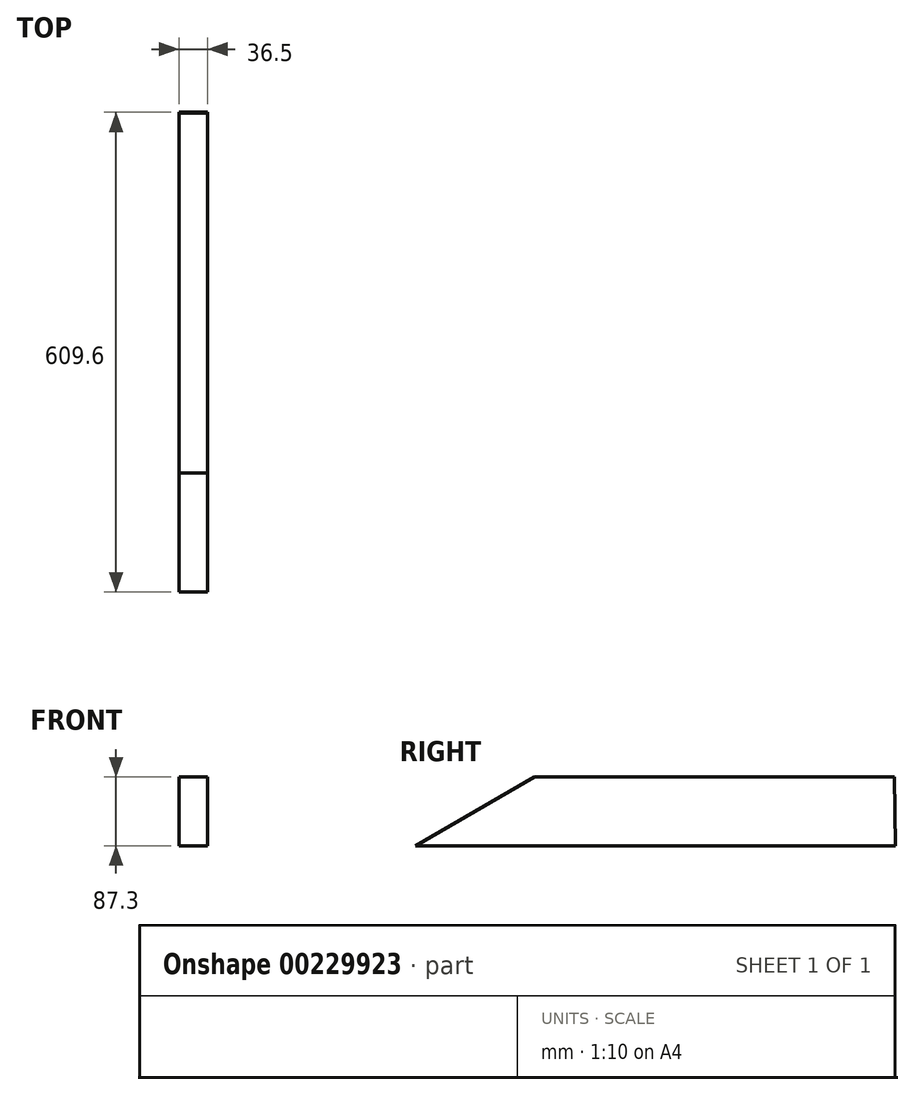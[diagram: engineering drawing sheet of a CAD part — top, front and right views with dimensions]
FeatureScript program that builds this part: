
annotation { "Feature Type Name" : "Feature", "Feature Type Description" : "" }
export const myFeature = defineFeature(function(context is Context, id is Id, definition is map)
    precondition{}
    {
        {
            var Q0;
            Q0=qCreatedBy(makeId("Right.planeOp"),FACE);
            var sketch = newSketch(context, id + "F0", { "sketchPlane" : qUnion([Q0])});
            skLineSegment(sketch, "E0.bottom", {"start": v(-229.2, 43.65) * mm, "end": v(228, 43.65) * mm});
            skLineSegment(sketch, "E0.top", {"start": v(13.52, -43.65) * mm, "end": v(229.2, -43.65) * mm});
            skLineSegment(sketch, "E0.right", {"start": v(228, 43.65) * mm, "end": v(229.2, -43.65) * mm});
            skLineSegment(sketch, "E1", {"start": v(-229.2, 43.65) * mm, "end": v(-380.4, -43.65) * mm});
            skLineSegment(sketch, "E2", {"start": v(13.52, -43.65) * mm, "end": v(-380.4, -43.65) * mm});
            skLineSegment(sketch, "E3", {"start": v(-229.2, 43.65) * mm, "end": v(229.2, -43.65) * mm, "construction": true});
            skSolve(sketch);
        }
        {
            var Q0;
            Q0=makeQuery(id+"F0.imprint","IMPRINT",FACE,{"disambiguationData":[TD([[makeQuery(id+"F0.imprint","IMPRINT",EDGE,{"derivedFrom":sQuery(id+"F0.wireOp",EDGE,"E0.bottom")}),-1.0]])]});
            extrude(context, id + "F1", {"entities" : qUnion([Q0]), "depth" : 36.5 * mm});
        }
    });
